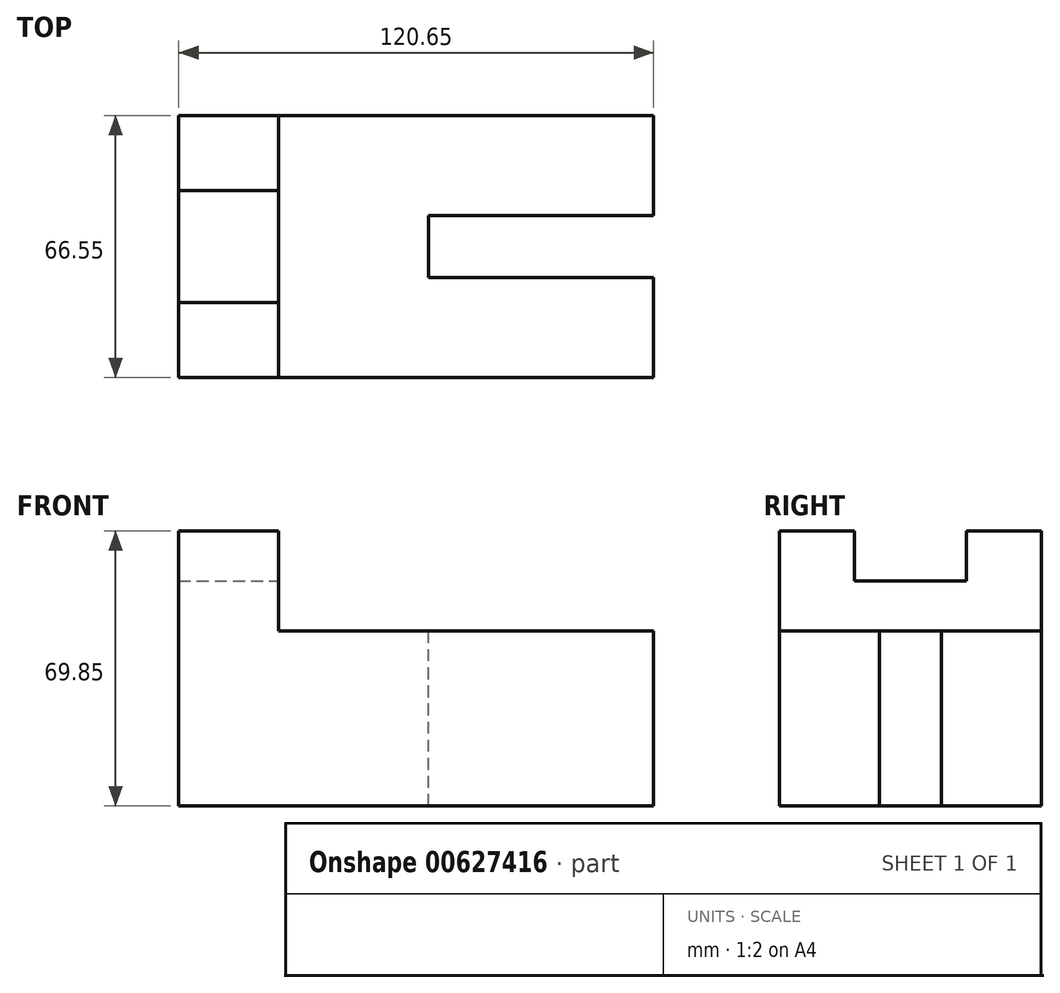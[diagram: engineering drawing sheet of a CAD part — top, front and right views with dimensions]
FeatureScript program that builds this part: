
annotation { "Feature Type Name" : "Feature", "Feature Type Description" : "" }
export const myFeature = defineFeature(function(context is Context, id is Id, definition is map)
    precondition{}
    {
        {
            var Q0;
            Q0=qCreatedBy(makeId("Top.planeOp"),FACE);
            var sketch = newSketch(context, id + "F0", { "sketchPlane" : qUnion([Q0])});
            skLineSegment(sketch, "E0.bottom", {"start": v(0, 0) * mm, "end": v(120.65, 0) * mm});
            skLineSegment(sketch, "E0.top", {"start": v(0, -66.55) * mm, "end": v(120.65, -66.55) * mm});
            skLineSegment(sketch, "E0.left", {"start": v(0, 0) * mm, "end": v(0, -66.55) * mm});
            skLineSegment(sketch, "E0.right", {"start": v(120.65, 0) * mm, "end": v(120.65, -66.55) * mm});
            skSolve(sketch);
        }
        {
            var Q0;
            Q0=makeQuery(id+"F0.imprint","IMPRINT",FACE,{"disambiguationData":[TD([[makeQuery(id+"F0.imprint","IMPRINT",EDGE,{"derivedFrom":sQuery(id+"F0.wireOp",EDGE,"E0.bottom")}),-1.0]])]});
            extrude(context, id + "F1", {"entities" : qUnion([Q0]), "depth" : 19.05 * mm, "offsetDistance" : 25.4 * mm});
        }
        {
            var Q0;
            Q0=makeQuery(id+"F1.opExtrude","SWEPT_FACE",FACE,{"disambiguationData":[OSD([sQuery(id+"F0.wireOp",EDGE,"E0.top")])]});
            var sketch = newSketch(context, id + "F2", { "sketchPlane" : qUnion([Q0])});
            skLineSegment(sketch, "E1.bottom", {"start": v(0, 0) * mm, "end": v(25.4, 0) * mm});
            skLineSegment(sketch, "E1.top", {"start": v(0, 44.45) * mm, "end": v(25.4, 44.45) * mm});
            skLineSegment(sketch, "E1.left", {"start": v(0, 0) * mm, "end": v(0, 44.45) * mm});
            skLineSegment(sketch, "E1.right", {"start": v(25.4, 0) * mm, "end": v(25.4, 44.45) * mm});
            skSolve(sketch);
        }
        {
            var Q0;
            Q0 = qSketchRegion(id + "F2", true);
            extrude(context, id + "F3", {"entities" : qUnion([Q0]), "operationType" : NewBodyOperationType.ADD, "oppositeDirection" : true, "depth" : 66.55 * mm, "offsetDistance" : 25.4 * mm});
        }
        {
            var Q0;
            Q0=makeQuery(id+"F3.opExtrude","SWEPT_FACE",FACE,{"disambiguationData":[OSD([sQuery(id+"F2.wireOp",EDGE,"E1.top")])]});
            var sketch = newSketch(context, id + "F4", { "sketchPlane" : qUnion([Q0])});
            skSolve(sketch);
        }
        {
            var Q0;
            {var subQ0=sQuery(id+"F2.wireOp",EDGE,"E1.top");Q0=makeQuery(id+"F4.imprint","IMPRINT",FACE,{"disambiguationData":[TD([[makeQuery(id+"F4.imprint","IMPRINT",EDGE,{"derivedFrom":makeQuery(id+"F3.opExtrude","CAP_EDGE",EDGE,{"disambiguationData":[OSD([subQ0])],"isStart":true})}),1.0]])]});}
            extrude(context, id + "F5", {"entities" : qUnion([Q0]), "operationType" : NewBodyOperationType.ADD, "depth" : 25.4 * mm, "offsetDistance" : 25.4 * mm});
        }
        {
            var Q0;
            Q0=makeQuery(id+"F5.opExtrude","CAP_FACE",FACE,{"disambiguationData":[OSD([sQuery(id+"F2.wireOp",EDGE,"E1.top"),sQuery(id+"F2.wireOp",EDGE,"E1.left"),sQuery(id+"F2.wireOp",EDGE,"E1.right")])],"isStart":false});
            var sketch = newSketch(context, id + "F6", { "sketchPlane" : qUnion([Q0])});
            skLineSegment(sketch, "E2.bottom", {"start": v(0, 0) * mm, "end": v(25.4, 0) * mm});
            skLineSegment(sketch, "E2.top", {"start": v(0, -19.45) * mm, "end": v(25.4, -19.45) * mm});
            skLineSegment(sketch, "E2.left", {"start": v(0, 0) * mm, "end": v(0, -19.45) * mm});
            skLineSegment(sketch, "E2.right", {"start": v(25.4, 0) * mm, "end": v(25.4, -19.45) * mm});
            skLineSegment(sketch, "E3.bottom", {"start": v(0, -66.55) * mm, "end": v(25.4, -66.55) * mm});
            skLineSegment(sketch, "E3.top", {"start": v(0, -47.5) * mm, "end": v(25.4, -47.5) * mm});
            skLineSegment(sketch, "E3.left", {"start": v(0, -66.55) * mm, "end": v(0, -47.5) * mm});
            skLineSegment(sketch, "E3.right", {"start": v(25.4, -66.55) * mm, "end": v(25.4, -47.5) * mm});
            skSolve(sketch);
        }
        {
            var Q0;
            {var subQ0=sQuery(id+"F6.wireOp",EDGE,"E2.top");Q0=makeQuery(id+"F6.imprint","IMPRINT",FACE,{"disambiguationData":[TD([[makeQuery(id+"F6.imprint","IMPRINT",EDGE,{"derivedFrom":subQ0}),-1.0]])]});}
            extrude(context, id + "F7", {"entities" : qUnion([Q0]), "operationType" : NewBodyOperationType.ADD, "oppositeDirection" : true, "depth" : 12.7 * mm, "offsetDistance" : 25.4 * mm});
        }
        {
            var Q0;
            Q0=makeQuery(id+"F5.opExtrude","CAP_FACE",FACE,{"disambiguationData":[OSD([sQuery(id+"F2.wireOp",EDGE,"E1.top"),sQuery(id+"F2.wireOp",EDGE,"E1.left"),sQuery(id+"F2.wireOp",EDGE,"E1.right")])],"isStart":false});
            var sketch = newSketch(context, id + "F8", { "sketchPlane" : qUnion([Q0])});
            skLineSegment(sketch, "E4", {"start": v(0, 0) * mm, "end": v(0, -19.05) * mm});
            skLineSegment(sketch, "E5", {"start": v(0, -66.55) * mm, "end": v(0, -47.5) * mm});
            skLineSegment(sketch, "E6.bottom", {"start": v(0, -19.05) * mm, "end": v(25.4, -19.05) * mm});
            skLineSegment(sketch, "E6.top", {"start": v(0, -47.5) * mm, "end": v(25.4, -47.5) * mm});
            skLineSegment(sketch, "E6.left", {"start": v(0, -19.05) * mm, "end": v(0, -47.5) * mm});
            skLineSegment(sketch, "E6.right", {"start": v(25.4, -19.05) * mm, "end": v(25.4, -47.5) * mm});
            skSolve(sketch);
        }
        {
            var Q0;
            Q0 = qSketchRegion(id + "F8", true);
            extrude(context, id + "F9", {"entities" : qUnion([Q0]), "operationType" : NewBodyOperationType.REMOVE, "oppositeDirection" : true, "depth" : 12.7 * mm, "offsetDistance" : 25.4 * mm});
        }
        {
            var Q0;
            Q0=makeQuery(id+"F1.opExtrude","CAP_FACE",FACE,{"disambiguationData":[OSD([sQuery(id+"F0.wireOp",EDGE,"E0.bottom"),sQuery(id+"F0.wireOp",EDGE,"E0.top"),sQuery(id+"F0.wireOp",EDGE,"E0.left"),sQuery(id+"F0.wireOp",EDGE,"E0.right")])],"isStart":false});
            var sketch = newSketch(context, id + "F10", { "sketchPlane" : qUnion([Q0])});
            skLineSegment(sketch, "E7", {"start": v(120.65, -66.55) * mm, "end": v(120.65, -41.15) * mm});
            skLineSegment(sketch, "E8", {"start": v(120.65, -41.15) * mm, "end": v(63.5, -41.15) * mm});
            skLineSegment(sketch, "E9", {"start": v(120.65, 0) * mm, "end": v(120.65, -25.4) * mm});
            skLineSegment(sketch, "E10", {"start": v(120.65, -25.4) * mm, "end": v(63.5, -25.4) * mm});
            skLineSegment(sketch, "E11", {"start": v(63.5, -25.4) * mm, "end": v(63.5, -41.15) * mm});
            skSolve(sketch);
        }
        {
            var Q0;
            {var subQ0=sQuery(id+"F10.wireOp",EDGE,"E8");Q0=makeQuery(id+"F10.imprint","IMPRINT",FACE,{"disambiguationData":[TD([[makeQuery(id+"F10.imprint","IMPRINT",EDGE,{"derivedFrom":subQ0}),-1.0]])]});}
            extrude(context, id + "F11", {"entities" : qUnion([Q0]), "operationType" : NewBodyOperationType.REMOVE, "oppositeDirection" : true, "depth" : 25.4 * mm, "offsetDistance" : 25.4 * mm});
        }
        {
            var Q0;
            Q0=makeQuery(id+"F1.opExtrude","CAP_FACE",FACE,{"disambiguationData":[OSD([sQuery(id+"F0.wireOp",EDGE,"E0.bottom"),sQuery(id+"F0.wireOp",EDGE,"E0.top"),sQuery(id+"F0.wireOp",EDGE,"E0.left"),sQuery(id+"F0.wireOp",EDGE,"E0.right")])],"isStart":false});
            var sketch = newSketch(context, id + "F12", { "sketchPlane" : qUnion([Q0])});
            skLineSegment(sketch, "E12", {"start": v(0, 0) * mm, "end": v(88.9, 0) * mm});
            skLineSegment(sketch, "E13", {"start": v(88.9, 0) * mm, "end": v(120.65, 0) * mm});
            skLineSegment(sketch, "E14.0", {"start": v(88.9, -762) * mm, "end": v(120.65, -762) * mm});
            skSolve(sketch);
        }
        {
            var Q0;
            {var subQ6=sQuery(id+"F12.wireOp",EDGE,"E13");Q0=makeQuery(id+"F12.imprint","IMPRINT",FACE,{"disambiguationData":[TD([[makeQuery(id+"F12.imprint","IMPRINT",EDGE,{"derivedFrom":subQ6}),-1.0]])]});}
            extrude(context, id + "F13", {"entities" : qUnion([Q0]), "operationType" : NewBodyOperationType.ADD, "depth" : 25.4 * mm, "offsetDistance" : 25.4 * mm});
        }
    });
